# Revit family: VE_Exhaust Unit_F_MEPcontent_ClimaRad_MaxiBox
name_source: partatom
category: Mechanical Equipment
revit_build: Autodesk Revit 2018 (Build: 20170223_1515(x64)
units: mm (PartAtom-declared; Revit-internal decimal feet)

## family parameters
Cut with Voids When Loaded = No
Host = Face
OmniClass Number = 23.75.70.21.31
OmniClass Title = Exhaust Terminals
Part Type = Normal
Room Calculation Point = Yes
Round Connector Dimension = Use Radius
Shared = No

## types (1)
- MaxiBox
    Article Description = Exhaust unit
    Article Type = MaxiBox
    Base Family Version = 12.19
    Blue = Color RGB 0-168-255
    Content Supplier URL = www.MEPcontent.com
    Custom = No
    Dark Grey = Color RGB 59-56-56
    Default Elevation = 0 mm  [stored 0 ft]
    Depth = 303 mm  [stored 0.994094 ft]
    Description = Exhaust unit
    EMCS Version = 4.0
    ETIM Article Class = EC001462
    Family Version = 10.04
    Height = 463 mm  [stored 1.51903 ft]
    IFCExportAs = IfcAirTerminalBox
    IFCExportType = NOTDEFINED
    Light Grey = Color RGB 214-214-214
    MEPcontent Class = EXHAUST_UNIT
    Manufacturer = ClimaRad
    Manufacturer Art. No. = 4610100
    Manufacturer URL = www.climarad.com
    Maximum Flow = 83.3 L/s
    Model = MaxiBox
    Power = 65 VA
    Product Line = ClimaRad
    Radius Exhaust Air = 63 mm
    Revit Version = 2018
    URL = https://mep.trimble.com
    Voltage = 230 V
    Width = 442 mm  [stored 1.45013 ft]

note: [stored X ft] marks values corroborated as IEEE doubles in the binary element streams (Revit-internal decimal feet)

## geometry (parser evidence)
native form markers: Sweep x5
no freeform markers — native parametric forms only
